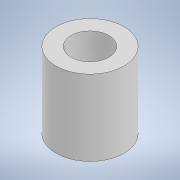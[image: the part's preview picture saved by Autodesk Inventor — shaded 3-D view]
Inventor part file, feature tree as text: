
AUTODESK INVENTOR PART (.ipt)
format: ipt  version: 2022.3 (Build 263350000, 350)  size: 98,304 bytes
history: native  units: mm
features: extrude x1, sketch x1
ambient origin geometry x8: Origin, YZ Plane, XZ Plane, XY Plane, X Axis, Y Axis, Z Axis, Center Point
bodies: Solid1 (feature_tree)
feature tree (2):
  extrude  "Extrusion1"  Depth=10.0mm
  sketch  "Sketch1"  dims[d0=5.0mm d1=2.0mm d2=10.0mm d3=0.0mm]
